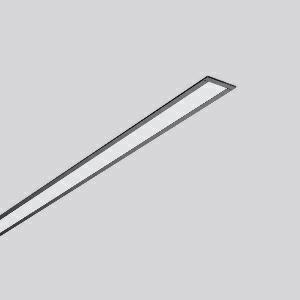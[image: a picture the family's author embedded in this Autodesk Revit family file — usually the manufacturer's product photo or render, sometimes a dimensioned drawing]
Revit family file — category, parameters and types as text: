
# Revit family: less_is_more_27_312176_003_76_bc47
name_source: partatom
category: Lighting Fixtures
units: mm (PartAtom-declared; Revit-internal decimal feet)

## family parameters
Cut with Voids When Loaded = No
Host = Face
Light Source = No
Part Type = Normal
Room Calculation Point = No
Round Connector Dimension = Use Diameter
Shared = No

## types (1)
- LESS IS MORE 27 (1 x LED Modul 830, 1600 lm, 3000)
    Apparent Load = 29 VA
    CIE Flux Codes = 48 79 96 100 100
    Color Rendering = 80
    Color Temperature = 3000
    Default Elevation = 1800 mm
    Description = Series: LESS IS MORE 27
Recessed ceiling and wall luminaire with slim design. Housing: extruded aluminium profile, powder-coated. End cap aluminium powder-coated. Diffuser made of non-yellowing plastic (PMMA), opal. Suitable for Recessed ceiling mounting, wall (recessed). External driver with connecting cable. 
Colour: deep black, matt (RAL 9005)
Length: 1014 mm
Width: 38 mm
Height: 2 mm
Cut-out length: 1006 mm
Cut-out width: 30 mm
Recess height: 45-60 mm
Luminaire: recess height: 37 mm
Lamp: LED
Socket: without socket
Colour temperature: 3000K
Colour rendering index (CRI): 82
System power: 29 W
Rated luminous flux: 1600 lm
Luminous efficiency: 55 lm/W
Control gear: Voltage converter, DALI dim.
Protection class: II
Type of protection: IP 20
    Height = 0 mm  [stored 0 ft]
    Lamp = 1 x LED Modul 830
    Lamp Light Flux = 1600 lm
    Lamp count = 1
    Length = 1014 mm
    Lifetime = 50000 h
    Luminous efficacy = 55 lm/W
    Manufacturer = RZB
    ModVariant = No
    Model = 312176.003.76
    Mounting Place = Ceiling, Wall
    Mounting Type = Recessed
    Number of Poles = 1
    OnlyDefault = Yes
    Power Factor = 1
    Product Name = LESS IS MORE 27
    Product group = Recessed LED linear luminaires
    ProductGroupID = 407
    Protection Class = Protection class II
    Protection Degree = IP 20
    RLX_Detail_Level = 1
    RLX_Emergency_Light_Flux = 0 lm
    RLX_Emergency_Type = 0
    RLX_Emergency_Type_DB = No
    RlxData = <blob elided: 26105 chars, md5=06a8ae2e>
    Socket = socket
    Standby Power = 0 W
    System Light Flux = 1600 lm
    System Power = 29 W
    Type Comments = Product without accessories
    Type Image = 312176.003.jpg
    URL = http://relux.com
    VarID = ---
    Voltage = 230 V
    Voltage Range = 220-240 V
    Weight = 0.00 kg
    Width = 38 mm

note: [stored X ft] marks values corroborated as IEEE doubles in the binary element streams (Revit-internal decimal feet)

## geometry (parser evidence)
native form markers: Blend x4, Sweep x11
no freeform markers — native parametric forms only
